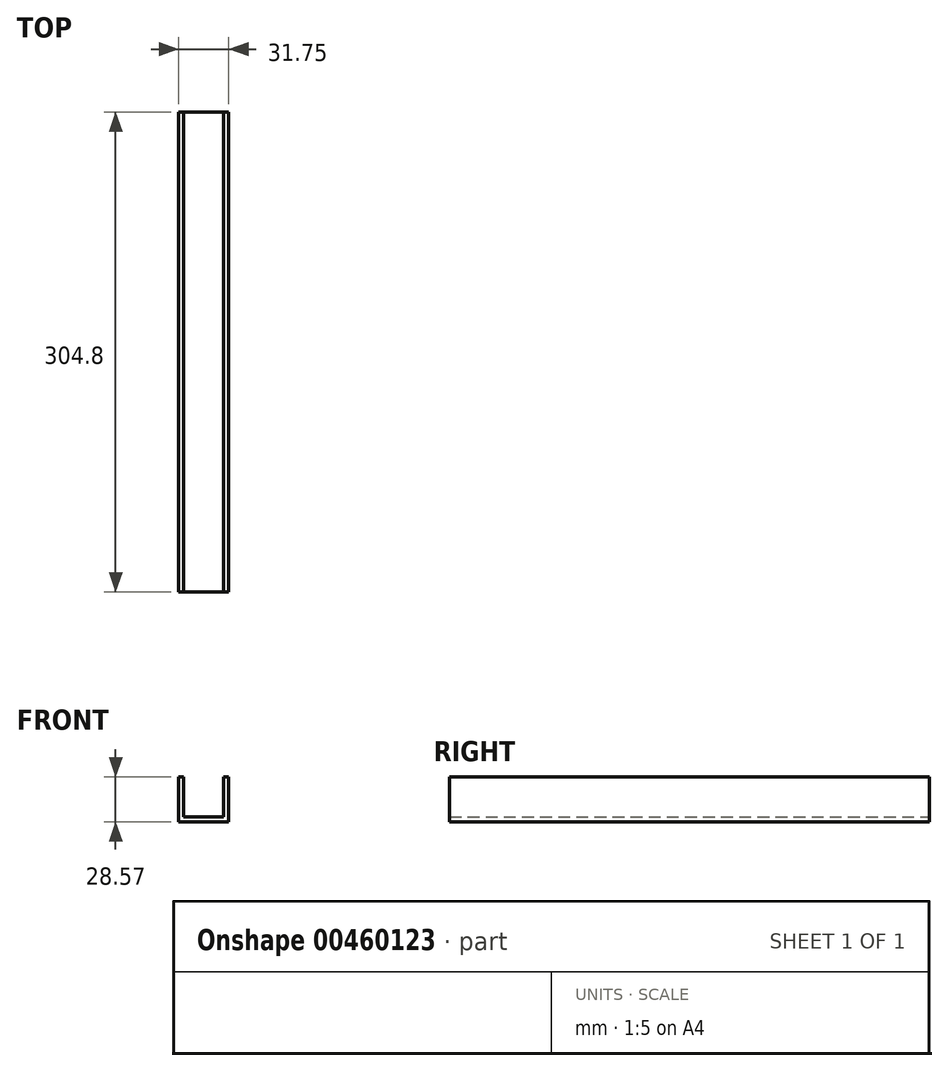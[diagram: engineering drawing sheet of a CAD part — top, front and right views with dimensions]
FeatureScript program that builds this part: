
annotation { "Feature Type Name" : "Feature", "Feature Type Description" : "" }
export const myFeature = defineFeature(function(context is Context, id is Id, definition is map)
    precondition{}
    {
        {
            var Q0;
            Q0=qCreatedBy(makeId("Front.planeOp"),FACE);
            var sketch = newSketch(context, id + "F0", { "sketchPlane" : qUnion([Q0])});
            skLineSegment(sketch, "E0", {"start": v(0, 0) * mm, "end": v(31.75, 0) * mm});
            skLineSegment(sketch, "E1", {"start": v(31.75, 0) * mm, "end": v(31.75, 28.58) * mm});
            skLineSegment(sketch, "E2", {"start": v(31.75, 28.58) * mm, "end": v(28.57, 28.58) * mm});
            skLineSegment(sketch, "E3", {"start": v(28.57, 28.58) * mm, "end": v(28.57, 3.18) * mm});
            skLineSegment(sketch, "E4", {"start": v(28.58, 3.18) * mm, "end": v(3.18, 3.17) * mm});
            skLineSegment(sketch, "E5", {"start": v(3.18, 3.18) * mm, "end": v(3.18, 28.58) * mm});
            skLineSegment(sketch, "E6", {"start": v(3.18, 28.58) * mm, "end": v(0, 28.58) * mm});
            skLineSegment(sketch, "E7", {"start": v(0, 28.58) * mm, "end": v(0, 0) * mm});
            skSolve(sketch);
        }
        {
            var Q0;
            Q0=makeQuery(id+"F0.imprint","IMPRINT",FACE,{"disambiguationData":[TD([[makeQuery(id+"F0.imprint","IMPRINT",EDGE,{"derivedFrom":sQuery(id+"F0.wireOp",EDGE,"E0")}),1.0]])]});
            extrude(context, id + "F1", {"entities" : qUnion([Q0]), "depth" : 304.8 * mm, "offsetDistance" : 25.4 * mm});
        }
    });
